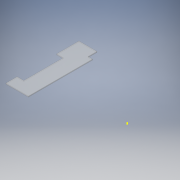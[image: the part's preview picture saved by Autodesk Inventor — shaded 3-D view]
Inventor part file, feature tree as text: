
AUTODESK INVENTOR PART (.ipt)
format: ipt  version: 2016 (Build 200138000, 138)  size: 158,208 bytes
history: native  units: in
note: dims shown in document units (in); Inventor stores cm internally (conversion verified against a paired STEP export)
features: sketch x10, extrude x6
ambient origin geometry x8: Origin, YZ Plane, XZ Plane, XY Plane, X Axis, Y Axis, Z Axis, Center Point
bodies: Solid1 (feature_tree)
feature tree (16):
  extrude  "Extrusion1"  Depth=5.0in
  sketch  "Sketch2"  dims[d3=5.0in d4=1.5in]
  extrude  "Extrusion2"  Depth=1.5in
  sketch  "Sketch4"  dims[d9=0.75in d11=2.0in]
  sketch  "Sketch5"  dims[d12=1.6875in d13=0.0in d14=1.125in d15=0.0in]
  sketch  "Sketch6"  dims[d16=0.25in d17=1.4375in d18=0.0in]
  extrude  "Extrusion3"  Depth=4.875in TaperAngle=0.0deg
  extrude  "Extrusion4"  Depth=2.0in
  extrude  "Extrusion5"  Depth=1.125in TaperAngle=0.0deg
  sketch  "Sketch9"
  extrude  "Extrusion6"  Depth=1.4375in TaperAngle=0.0deg
  sketch  "Sketch1"  dims[d0=0.187in d1=0.0in d2=5.0in]
  sketch  "Sketch3"  dims[d5=2.5625in d6=0.0in d7=4.875in d8=0.0in]
  sketch  "Sketch7"
  sketch  "Sketch8"
  sketch  "Sketch10"
